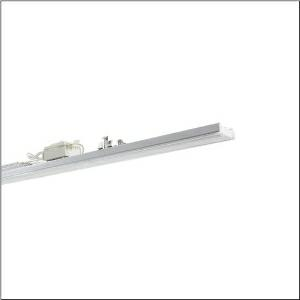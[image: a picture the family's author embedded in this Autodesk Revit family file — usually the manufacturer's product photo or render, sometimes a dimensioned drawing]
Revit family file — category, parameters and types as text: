
# Revit family: licross_r__21_recessed_mo_52tl14cn485g_d932
name_source: partatom
category: Lighting Fixtures
units: mm (PartAtom-declared; Revit-internal decimal feet)

## family parameters
Cut with Voids When Loaded = No
Host = Face
Light Source = No
Part Type = Normal
Room Calculation Point = No
Round Connector Dimension = Use Diameter
Shared = No

## types (1)
- --- (1 x LED, 8530 lm, 49.9 W, 4000K)
    Apparent Load = 50 VA
    CIE Flux Codes = 56 84 97 100 100
    Color Rendering = 80
    Color Temperature = 4000K
    Default Elevation = 1800 mm
    Description = Licross® 21 Recessed MO, luminaire insert, of sheet steel, galvanised, coil coated, white, length: 1.500mm, width: 66mm, height: 67mm, LED rated luminous flux: 8.530lm, light colour: 840, control gear: ON/OFF Multilumen, CLOi, control gear: ECG DALI, with plug, 5-pole, with phase selection, mains connection: 220..240V, AC, 50/60Hz, start of lifetime: 50W, end of service life: 61W, halogen-free wiring, primary light control with lens, of plastic, primary optical cover: cover, of PMMA, light emission: direct distribution, primary light characteristic: asymmetric, protection rating (complete): IP40, insulation class (complete): insulation class I (protective earthing), certification: CE, ENEC, VDE, UKCA, protection symbol: D if used in an environment without relevant dust loads with corresponding accessories, impact resistance: IK06, permissible ambient temperature for indoor applications: -35..+40°C, corresponds to IFS (International Featured Standards) requirements for safety and quality in the food industry, reducing of maximum allowable ambient temperature of 5°C with ceiling mounting, LABS conformity tested according to VDMA 24364:2018-05, packaging unit: 1 piece
    Height = 58 mm
    Lamp = 1 x LED
    Lamp Light Flux = 8530 lm
    Lamp Power = 49.9 W
    Lamp count = 1
    Length = 1500 mm
    Luminous efficacy = 171 lm/W
    Manufacturer = Siteco
    ModVariant = No
    Model = 52TL14CN485G
    Mounting Place = Ceiling
    Mounting Type = Pendant
    Number of Poles = 1
    OnlyDefault = Yes
    Power Factor = 1
    Product Name = Licross® 21 Recessed MO
    Product group = luminaire insert
    ProductGroupID = 902
    Protection Class = Protection class I
    Protection Degree = IP 40
    RLX_Detail_Level = 1
    RLX_Emergency_Light_Flux = 0 lm
    RLX_Emergency_Type = 0
    RLX_Emergency_Type_DB = No
    RlxData = <blob elided: 22773 chars, md5=bdde6988>
    Socket = socket
    Standby Power = 0 W
    System Light Flux = 8530 lm
    System Power = 50 W
    Type Comments = factory setting: luminous flux: 100 % | (A | C | E) | 116 mA
    Type Image = l_1296930.jpg
    URL = http://relux.com
    VarID = @adj_110782
    Voltage = 0 V
    Weight = 0.00 kg
    Width = 66 mm

## geometry (parser evidence)
native form markers: Blend x4, Sweep x9
no freeform markers — native parametric forms only
